# Revit family: UV Low Pressure - Control Panel
name_source: partatom
category: Mechanical Equipment
units: mm (PartAtom-declared; Revit-internal decimal feet)

## family parameters
Always vertical = Yes
Cut with Voids When Loaded = No
OmniClass Number = 23.65.50.11
OmniClass Title = Water Treatment
Part Type = Normal
Room Calculation Point = No
Round Connector Dimension = Use Radius
Shared = No
Work Plane-Based = No

## types (4) — shared parameters
Assembly Code = D2090400
Description = Jandy Commercial Low-Pressure UV System
Fluidra_Cos ϕ = 100.00%
Fluidra_Description = Jandy Commercial Low-Pressure UV System
Fluidra_Frequency = 60 Hz
Fluidra_Manufacturer = Fluidra
Fluidra_Phase = 1
Fluidra_Voltage (High) = 240 V
Fluidra_Voltage (Low) = 120 V
Manufacturer = Fluidra
URL = https://www.jandy.com

## per-type parameters (varying)
| type | Fluidra_#_Electronic_Ballasts | Fluidra_Current(120V) | Fluidra_Current(240V) | Fluidra_Model | Fluidra_Rated_Power | Fluidra_UV-C_Power | Model |
| JUVLP100 - Control Panel | 3 | 2 A | 1 A | JUVLP100 - Contol Panel | 270 W | 90 W | JUVLP100 - Contol Panel |
| JUVLP150 - Control Panel | 4 | 2 A | 1 A | JUVLP150 - Contol Panel | 360 W | 120 W | JUVLP150 - Contol Panel |
| JUVLP200 - Control Panel | 5 | 3 A | 2 A | JUVLP200 - Contol Panel | 450 W | 150 W | JUVLP200 - Contol Panel |
| JUVLP250 - Control Panel | 6 | 4 A | 2 A | JUVLP250 - Contol Panel | 540 W | 180 W | JUVLP250 - Contol Panel |

## geometry (parser evidence)
native form markers: Sweep x3
no freeform markers — native parametric forms only
